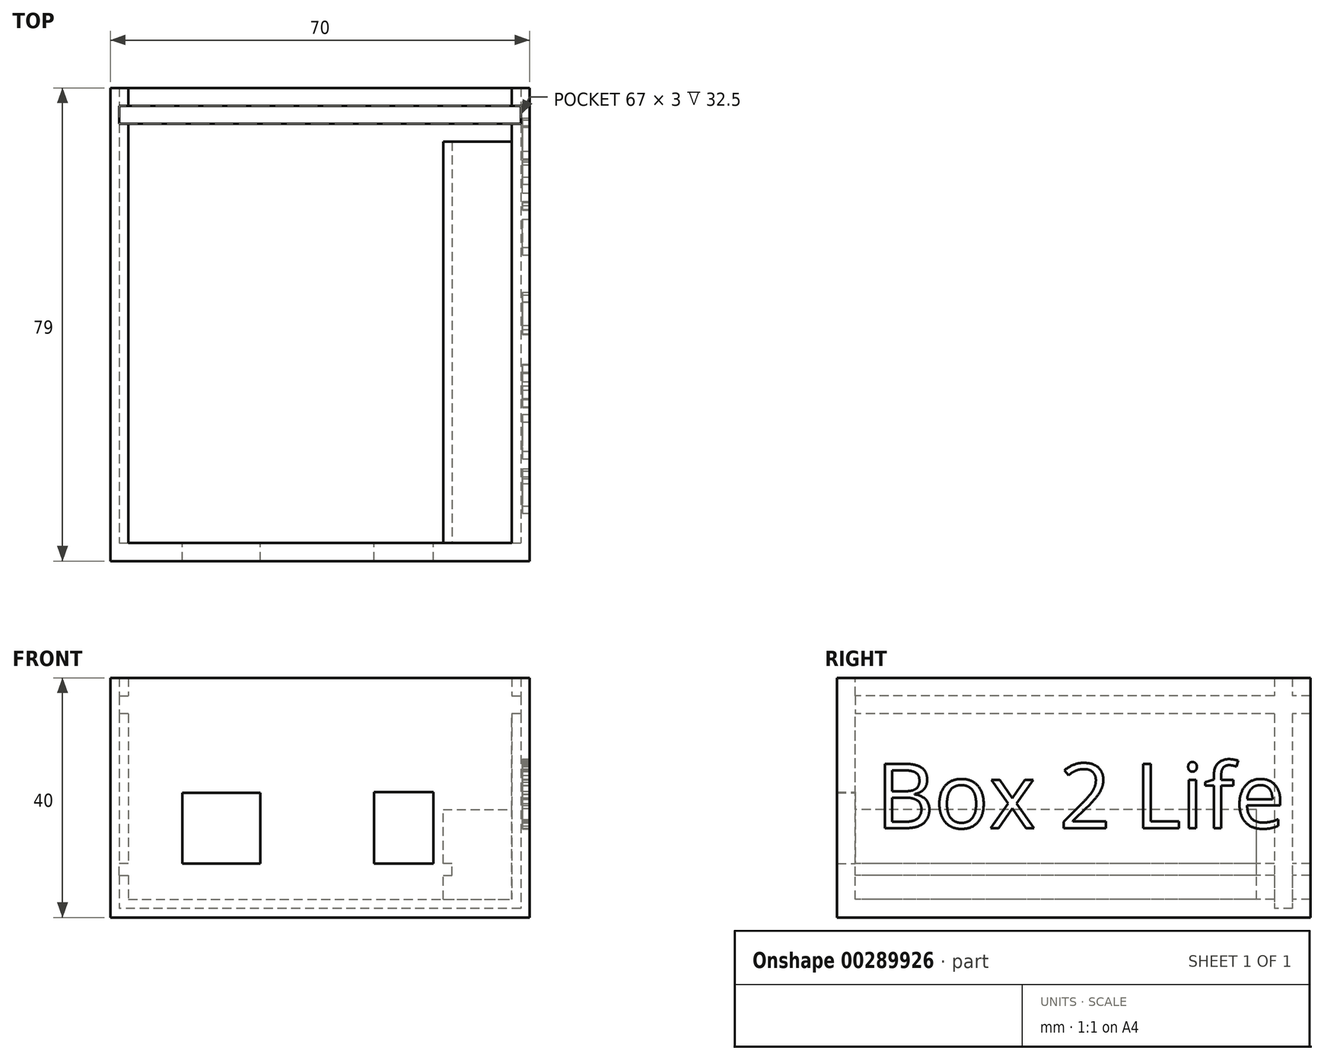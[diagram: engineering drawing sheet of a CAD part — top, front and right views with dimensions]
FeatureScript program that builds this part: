
annotation { "Feature Type Name" : "Feature", "Feature Type Description" : "" }
export const myFeature = defineFeature(function(context is Context, id is Id, definition is map)
    precondition{}
    {
        {
            var Q0;
            Q0=qCreatedBy(makeId("Front.planeOp"),FACE);
            var sketch = newSketch(context, id + "F0", { "sketchPlane" : qUnion([Q0])});
            skLineSegment(sketch, "E0.bottom", {"start": v(0, 0) * mm, "end": v(70, 0) * mm});
            skLineSegment(sketch, "E0.left", {"start": v(0, 0) * mm, "end": v(0, 40) * mm});
            skLineSegment(sketch, "E0.right", {"start": v(70, 0) * mm, "end": v(70, 40) * mm});
            skLineSegment(sketch, "E1.bottom", {"start": v(12.5, 20.3) * mm, "end": v(24.5, 20.3) * mm, "construction": true});
            skLineSegment(sketch, "E1.top", {"start": v(12.5, 9.5) * mm, "end": v(24.5, 9.5) * mm, "construction": true});
            skLineSegment(sketch, "E1.left", {"start": v(12.5, 20.3) * mm, "end": v(12.5, 9.5) * mm, "construction": true});
            skLineSegment(sketch, "E1.right", {"start": v(24.5, 20.3) * mm, "end": v(24.5, 9.5) * mm, "construction": true});
            skLineSegment(sketch, "E2.bottom", {"start": v(44.5, 20.44) * mm, "end": v(53.43, 20.44) * mm, "construction": true});
            skLineSegment(sketch, "E2.top", {"start": v(44.5, 9.5) * mm, "end": v(53.43, 9.5) * mm, "construction": true});
            skLineSegment(sketch, "E2.left", {"start": v(44.5, 20.44) * mm, "end": v(44.5, 9.5) * mm, "construction": true});
            skLineSegment(sketch, "E2.right", {"start": v(53.43, 20.44) * mm, "end": v(53.43, 9.5) * mm, "construction": true});
            skLineSegment(sketch, "E3.0", {"start": v(12, 20.8) * mm, "end": v(25, 20.8) * mm});
            skLineSegment(sketch, "E3.1", {"start": v(12, 20.8) * mm, "end": v(12, 9) * mm});
            skLineSegment(sketch, "E3.2", {"start": v(12, 9) * mm, "end": v(25, 9) * mm});
            skLineSegment(sketch, "E3.3", {"start": v(25, 20.8) * mm, "end": v(25, 9) * mm});
            skLineSegment(sketch, "E4.0", {"start": v(44, 20.94) * mm, "end": v(53.93, 20.94) * mm});
            skLineSegment(sketch, "E4.1", {"start": v(44, 20.94) * mm, "end": v(44, 9) * mm});
            skLineSegment(sketch, "E4.2", {"start": v(44, 9) * mm, "end": v(53.93, 9) * mm});
            skLineSegment(sketch, "E4.3", {"start": v(53.93, 20.94) * mm, "end": v(53.93, 9) * mm});
            skLineSegment(sketch, "E5.0", {"start": v(3, 3) * mm, "end": v(3, 7) * mm});
            skLineSegment(sketch, "E5.1", {"start": v(3, 3) * mm, "end": v(55.54, 3) * mm});
            skLineSegment(sketch, "E6", {"start": v(3, 7) * mm, "end": v(1.5, 7) * mm});
            skLineSegment(sketch, "E7", {"start": v(1.5, 7) * mm, "end": v(1.5, 9) * mm});
            skLineSegment(sketch, "E8", {"start": v(1.5, 9) * mm, "end": v(3, 9) * mm});
            skLineSegment(sketch, "E9", {"start": v(55.54, 3) * mm, "end": v(55.54, 7) * mm});
            skLineSegment(sketch, "E10", {"start": v(55.54, 7) * mm, "end": v(57.04, 7) * mm});
            skLineSegment(sketch, "E11", {"start": v(57.04, 7) * mm, "end": v(57.04, 9) * mm});
            skLineSegment(sketch, "E12", {"start": v(57.04, 9) * mm, "end": v(55.54, 9) * mm});
            skLineSegment(sketch, "E13", {"start": v(55.54, 9) * mm, "end": v(55.54, 18) * mm});
            skLineSegment(sketch, "E14", {"start": v(55.54, 18) * mm, "end": v(67, 18) * mm});
            skLineSegment(sketch, "E15", {"start": v(3, 9) * mm, "end": v(3, 34) * mm});
            skLineSegment(sketch, "E16", {"start": v(67, 18) * mm, "end": v(67, 34) * mm});
            skLineSegment(sketch, "E17", {"start": v(67, 40) * mm, "end": v(70, 40) * mm});
            skLineSegment(sketch, "E18", {"start": v(0, 40) * mm, "end": v(3, 40) * mm});
            skLineSegment(sketch, "E19", {"start": v(3, 37) * mm, "end": v(1.5, 37) * mm});
            skLineSegment(sketch, "E20", {"start": v(1.5, 37) * mm, "end": v(1.5, 34) * mm});
            skLineSegment(sketch, "E21", {"start": v(1.5, 34) * mm, "end": v(3, 34) * mm});
            skLineSegment(sketch, "E22.trimOffspring", {"start": v(3, 37) * mm, "end": v(3, 40) * mm});
            skLineSegment(sketch, "E23", {"start": v(67, 37) * mm, "end": v(68.5, 37) * mm});
            skLineSegment(sketch, "E24", {"start": v(68.5, 37) * mm, "end": v(68.5, 34) * mm});
            skLineSegment(sketch, "E25", {"start": v(68.5, 34) * mm, "end": v(67, 34) * mm});
            skLineSegment(sketch, "E26.trimOffspring", {"start": v(67, 37) * mm, "end": v(67, 40) * mm});
            skLineSegment(sketch, "E27", {"start": v(0, 40) * mm, "end": v(70, 40) * mm, "construction": true});
            skLineSegment(sketch, "E28", {"start": v(55.54, 3) * mm, "end": v(67, 3) * mm, "construction": true});
            skLineSegment(sketch, "E29", {"start": v(67, 3) * mm, "end": v(67, 18) * mm, "construction": true});
            skSolve(sketch);
        }
        {
            var Q0;
            Q0=makeQuery(id+"F0.imprint","IMPRINT",FACE,{"disambiguationData":[TD([[makeQuery(id+"F0.imprint","IMPRINT",EDGE,{"derivedFrom":sQuery(id+"F0.wireOp",EDGE,"E0.bottom")}),1.0]])]});
            extrude(context, id + "F1", {"entities" : qUnion([Q0]), "oppositeDirection" : true, "depth" : 67 * mm});
        }
        {
            var Q0;
            Q0=makeQuery(id+"F0.imprint","IMPRINT",FACE,{"disambiguationData":[TD([[makeQuery(id+"F0.imprint","IMPRINT",EDGE,{"derivedFrom":sQuery(id+"F0.wireOp",EDGE,"E0.bottom")}),1.0]])]});
            var sketch = newSketch(context, id + "F2", { "sketchPlane" : qUnion([Q0])});
            skLineSegment(sketch, "E30.0", {"start": v(0, 0) * mm, "end": v(0, 40) * mm});
            skLineSegment(sketch, "E31.0", {"start": v(0, 0) * mm, "end": v(70, 0) * mm});
            skLineSegment(sketch, "E32.0", {"start": v(70, 0) * mm, "end": v(70, 40) * mm});
            skLineSegment(sketch, "E33.0", {"start": v(0, 40) * mm, "end": v(70, 40) * mm});
            skLineSegment(sketch, "E34.0", {"start": v(12, 20.8) * mm, "end": v(25, 20.8) * mm});
            skLineSegment(sketch, "E35.0", {"start": v(12, 20.8) * mm, "end": v(12, 9) * mm});
            skLineSegment(sketch, "E36.0", {"start": v(12, 9) * mm, "end": v(25, 9) * mm});
            skLineSegment(sketch, "E37.0", {"start": v(25, 20.8) * mm, "end": v(25, 9) * mm});
            skLineSegment(sketch, "E38.0", {"start": v(44, 20.94) * mm, "end": v(44, 9) * mm});
            skLineSegment(sketch, "E39.0", {"start": v(44, 20.94) * mm, "end": v(53.93, 20.94) * mm});
            skLineSegment(sketch, "E40.0", {"start": v(53.93, 20.94) * mm, "end": v(53.93, 9) * mm});
            skLineSegment(sketch, "E41.0", {"start": v(44, 9) * mm, "end": v(53.93, 9) * mm});
            skSolve(sketch);
        }
        {
            var Q0;
            Q0 = qSketchRegion(id + "F2", true);
            extrude(context, id + "F3", {"entities" : qUnion([Q0]), "operationType" : NewBodyOperationType.ADD, "depth" : 3 * mm});
        }
        {
            var Q0;
            Q0=makeQuery(id+"F1.opExtrude","CAP_FACE",FACE,{"disambiguationData":[OSD([sQuery(id+"F0.wireOp",EDGE,"E0.bottom"),sQuery(id+"F0.wireOp",EDGE,"E0.left"),sQuery(id+"F0.wireOp",EDGE,"E0.right"),sQuery(id+"F0.wireOp",EDGE,"E5.0"),sQuery(id+"F0.wireOp",EDGE,"E5.1"),sQuery(id+"F0.wireOp",EDGE,"E6"),sQuery(id+"F0.wireOp",EDGE,"E7"),sQuery(id+"F0.wireOp",EDGE,"E8"),sQuery(id+"F0.wireOp",EDGE,"E9"),sQuery(id+"F0.wireOp",EDGE,"E10"),sQuery(id+"F0.wireOp",EDGE,"E11"),sQuery(id+"F0.wireOp",EDGE,"E12"),sQuery(id+"F0.wireOp",EDGE,"E13"),sQuery(id+"F0.wireOp",EDGE,"E14"),sQuery(id+"F0.wireOp",EDGE,"E15"),sQuery(id+"F0.wireOp",EDGE,"E16"),sQuery(id+"F0.wireOp",EDGE,"E17"),sQuery(id+"F0.wireOp",EDGE,"E18"),sQuery(id+"F0.wireOp",EDGE,"E19"),sQuery(id+"F0.wireOp",EDGE,"E20"),sQuery(id+"F0.wireOp",EDGE,"E21"),sQuery(id+"F0.wireOp",EDGE,"E22.trimOffspring"),sQuery(id+"F0.wireOp",EDGE,"E23"),sQuery(id+"F0.wireOp",EDGE,"E24"),sQuery(id+"F0.wireOp",EDGE,"E25"),sQuery(id+"F0.wireOp",EDGE,"E26.trimOffspring")])],"isStart":false});
            var sketch = newSketch(context, id + "F4", { "sketchPlane" : qUnion([Q0])});
            skLineSegment(sketch, "E42.0", {"start": v(-70, 0) * mm, "end": v(-70, 40) * mm});
            skLineSegment(sketch, "E43.0", {"start": v(-67, 40) * mm, "end": v(-70, 40) * mm});
            skLineSegment(sketch, "E44.0", {"start": v(-67, 37) * mm, "end": v(-67, 40) * mm});
            skLineSegment(sketch, "E45.0", {"start": v(-67, 37) * mm, "end": v(-68.5, 37) * mm});
            skLineSegment(sketch, "E46.0", {"start": v(-68.5, 37) * mm, "end": v(-68.5, 34) * mm});
            skLineSegment(sketch, "E47.0", {"start": v(-68.5, 34) * mm, "end": v(-67, 34) * mm});
            skLineSegment(sketch, "E48.0", {"start": v(-67, 18) * mm, "end": v(-67, 34) * mm});
            skLineSegment(sketch, "E49.0", {"start": v(-67, 3) * mm, "end": v(-67, 18) * mm});
            skLineSegment(sketch, "E50.0", {"start": v(-55.54, 3) * mm, "end": v(-67, 3) * mm});
            skLineSegment(sketch, "E51.0", {"start": v(-3, 3) * mm, "end": v(-55.54, 3) * mm});
            skLineSegment(sketch, "E52.0", {"start": v(-3, 3) * mm, "end": v(-3, 7) * mm});
            skLineSegment(sketch, "E53.0", {"start": v(-3, 7) * mm, "end": v(-1.5, 7) * mm});
            skLineSegment(sketch, "E54.0", {"start": v(-1.5, 7) * mm, "end": v(-1.5, 9) * mm});
            skLineSegment(sketch, "E55.0", {"start": v(-1.5, 9) * mm, "end": v(-3, 9) * mm});
            skLineSegment(sketch, "E56.0", {"start": v(-3, 9) * mm, "end": v(-3, 34) * mm});
            skLineSegment(sketch, "E57.0", {"start": v(-1.5, 34) * mm, "end": v(-3, 34) * mm});
            skLineSegment(sketch, "E58.0", {"start": v(-1.5, 37) * mm, "end": v(-1.5, 34) * mm});
            skLineSegment(sketch, "E59.0", {"start": v(-3, 37) * mm, "end": v(-1.5, 37) * mm});
            skLineSegment(sketch, "E60.0", {"start": v(-3, 37) * mm, "end": v(-3, 40) * mm});
            skLineSegment(sketch, "E61.0", {"start": v(0, 40) * mm, "end": v(-3, 40) * mm});
            skLineSegment(sketch, "E62.0", {"start": v(0, 0) * mm, "end": v(0, 40) * mm});
            skLineSegment(sketch, "E63.0", {"start": v(0, 0) * mm, "end": v(-70, 0) * mm});
            skSolve(sketch);
        }
        {
            var Q0;
            Q0 = qSketchRegion(id + "F4", true);
            extrude(context, id + "F5", {"entities" : qUnion([Q0]), "operationType" : NewBodyOperationType.ADD, "depth" : 9 * mm});
        }
        {
            var Q0;
            Q0=makeQuery(id+"F5.boolean.opBoolean","MERGE",FACE,{"derivedFrom":[makeQuery(id+"F1.opExtrude","SWEPT_FACE",FACE,{"disambiguationData":[OSD([sQuery(id+"F0.wireOp",EDGE,"E16")])]}),makeQuery(id+"F5.opExtrude","SWEPT_FACE",FACE,{"disambiguationData":[OSD([sQuery(id+"F4.wireOp",EDGE,"E48.0"),sQuery(id+"F4.wireOp",EDGE,"E49.0")])]})]});
            cPlane(context, id + "F6", {"entities" : qUnion([Q0]), "cplaneType" : CPlaneType.OFFSET, "offset" : 0 * mm, "width" : 150 * mm, "height" : 150 * mm});
        }
        {
            var Q0;
            Q0=qCreatedBy(id+"F6.planeOp",FACE);
            var sketch = newSketch(context, id + "F7", { "sketchPlane" : qUnion([Q0])});
            skLineSegment(sketch, "E64.0", {"start": v(-76, 0) * mm, "end": v(-76, 40) * mm, "construction": true});
            skLineSegment(sketch, "E65", {"start": v(-76, 40) * mm, "end": v(-73, 40) * mm, "construction": true});
            skLineSegment(sketch, "E66", {"start": v(-73, 40) * mm, "end": v(-73, 1.5) * mm});
            skLineSegment(sketch, "E67", {"start": v(-70, 40) * mm, "end": v(-70, 1.5) * mm});
            skLineSegment(sketch, "E68", {"start": v(-70, 40) * mm, "end": v(-73, 40) * mm});
            skLineSegment(sketch, "E69", {"start": v(-73, 1.5) * mm, "end": v(-70, 1.5) * mm});
            skSolve(sketch);
        }
        {
            var Q0;
            Q0 = qSketchRegion(id + "F7", true);
            extrude(context, id + "F8", {"entities" : qUnion([Q0]), "operationType" : NewBodyOperationType.REMOVE, "oppositeDirection" : true, "depth" : 1.5 * mm});
        }
        {
            var Q0;
            Q0=makeQuery(id+"F5.boolean.opBoolean","MERGE",FACE,{"derivedFrom":[makeQuery(id+"F1.opExtrude","SWEPT_FACE",FACE,{"disambiguationData":[OSD([sQuery(id+"F0.wireOp",EDGE,"E15")])]}),makeQuery(id+"F5.opExtrude","SWEPT_FACE",FACE,{"disambiguationData":[OSD([sQuery(id+"F4.wireOp",EDGE,"E56.0")])]})]});
            cPlane(context, id + "F9", {"entities" : qUnion([Q0]), "cplaneType" : CPlaneType.OFFSET, "offset" : 0 * mm, "width" : 150 * mm, "height" : 150 * mm});
        }
        {
            var Q0;
            Q0=qCreatedBy(id+"F9.planeOp",FACE);
            var sketch = newSketch(context, id + "F10", { "sketchPlane" : qUnion([Q0])});
            skPoint(sketch, "E70.0", {"position": v(70, 40) * mm});
            skLineSegment(sketch, "E71.bottom", {"start": v(70, 40) * mm, "end": v(73, 40) * mm});
            skLineSegment(sketch, "E71.left", {"start": v(70, 40) * mm, "end": v(70, 1.5) * mm});
            skLineSegment(sketch, "E72", {"start": v(73, 40) * mm, "end": v(73, 1.5) * mm});
            skLineSegment(sketch, "E73", {"start": v(73, 1.5) * mm, "end": v(70, 1.5) * mm});
            skSolve(sketch);
        }
        {
            var Q0;
            Q0 = qSketchRegion(id + "F10", true);
            extrude(context, id + "F11", {"entities" : qUnion([Q0]), "operationType" : NewBodyOperationType.REMOVE, "oppositeDirection" : true, "depth" : 1.5 * mm});
        }
        {
            var Q0;
            Q0=makeQuery(id+"F5.boolean.opBoolean","MERGE",FACE,{"derivedFrom":[makeQuery(id+"F1.opExtrude","SWEPT_FACE",FACE,{"disambiguationData":[OSD([sQuery(id+"F0.wireOp",EDGE,"E5.1")])]}),makeQuery(id+"F5.opExtrude","SWEPT_FACE",FACE,{"disambiguationData":[OSD([sQuery(id+"F4.wireOp",EDGE,"E50.0"),sQuery(id+"F4.wireOp",EDGE,"E51.0")])]})]});
            var sketch = newSketch(context, id + "F12", { "sketchPlane" : qUnion([Q0])});
            skPoint(sketch, "E74.0", {"position": v(3, 70) * mm});
            skPoint(sketch, "E75.0", {"position": v(68.5, 70) * mm});
            skLineSegment(sketch, "E76.bottom", {"start": v(3, 70) * mm, "end": v(68.5, 70) * mm});
            skLineSegment(sketch, "E76.top", {"start": v(3, 70) * mm, "end": v(68.5, 70) * mm});
            skLineSegment(sketch, "E76.left", {"start": v(3, 70) * mm, "end": v(3, 70) * mm});
            skLineSegment(sketch, "E76.right", {"start": v(68.5, 70) * mm, "end": v(68.5, 70) * mm});
            skLineSegment(sketch, "E77", {"start": v(3, 70) * mm, "end": v(3, 73) * mm});
            skLineSegment(sketch, "E78", {"start": v(3, 73) * mm, "end": v(68.5, 73) * mm});
            skLineSegment(sketch, "E79", {"start": v(68.5, 73) * mm, "end": v(68.5, 70) * mm});
            skSolve(sketch);
        }
        {
            var Q0;
            Q0 = qSketchRegion(id + "F12", true);
            extrude(context, id + "F13", {"entities" : qUnion([Q0]), "operationType" : NewBodyOperationType.REMOVE, "oppositeDirection" : true, "depth" : 1.5 * mm});
        }
        {
            var Q0;
            Q0=makeQuery(id+"F5.boolean.opBoolean","MERGE",FACE,{"derivedFrom":[makeQuery(id+"F3.boolean.opBoolean","MERGE",FACE,{"derivedFrom":[makeQuery(id+"F1.opExtrude","SWEPT_FACE",FACE,{"disambiguationData":[OSD([sQuery(id+"F0.wireOp",EDGE,"E0.right")])]}),makeQuery(id+"F3.opExtrude","SWEPT_FACE",FACE,{"disambiguationData":[OSD([sQuery(id+"F2.wireOp",EDGE,"E32.0")])]})]}),makeQuery(id+"F5.opExtrude","SWEPT_FACE",FACE,{"disambiguationData":[OSD([sQuery(id+"F4.wireOp",EDGE,"E42.0")])]})]});
            var sketch = newSketch(context, id + "F14", { "sketchPlane" : qUnion([Q0])});
            skText(sketch, "E80", { "text": "Box 2 Life", "fontName": "OpenSans-Regular.ttf"});
            const initialGuessF14  = {"E80": [0.00348, 0.01492, 1, 0, 0.01083]};
            skSetInitialGuess(sketch, initialGuessF14);
            skSolve(sketch);
        }
        {
            var Q0;
            Q0 = qSketchRegion(id + "F14", true);
            var Q1;
            Q1 = qConstructionFilter(qBodyType(qCreatedBy(id + "F14" ,EDGE), BodyType.WIRE), ConstructionObject.NO);
            extrude(context, id + "F15", {"entities" : qUnion([Q0]), "operationType" : NewBodyOperationType.REMOVE, "surfaceEntities" : qUnion([Q1]), "oppositeDirection" : true, "depth" : 1.2 * mm});
        }
    });
